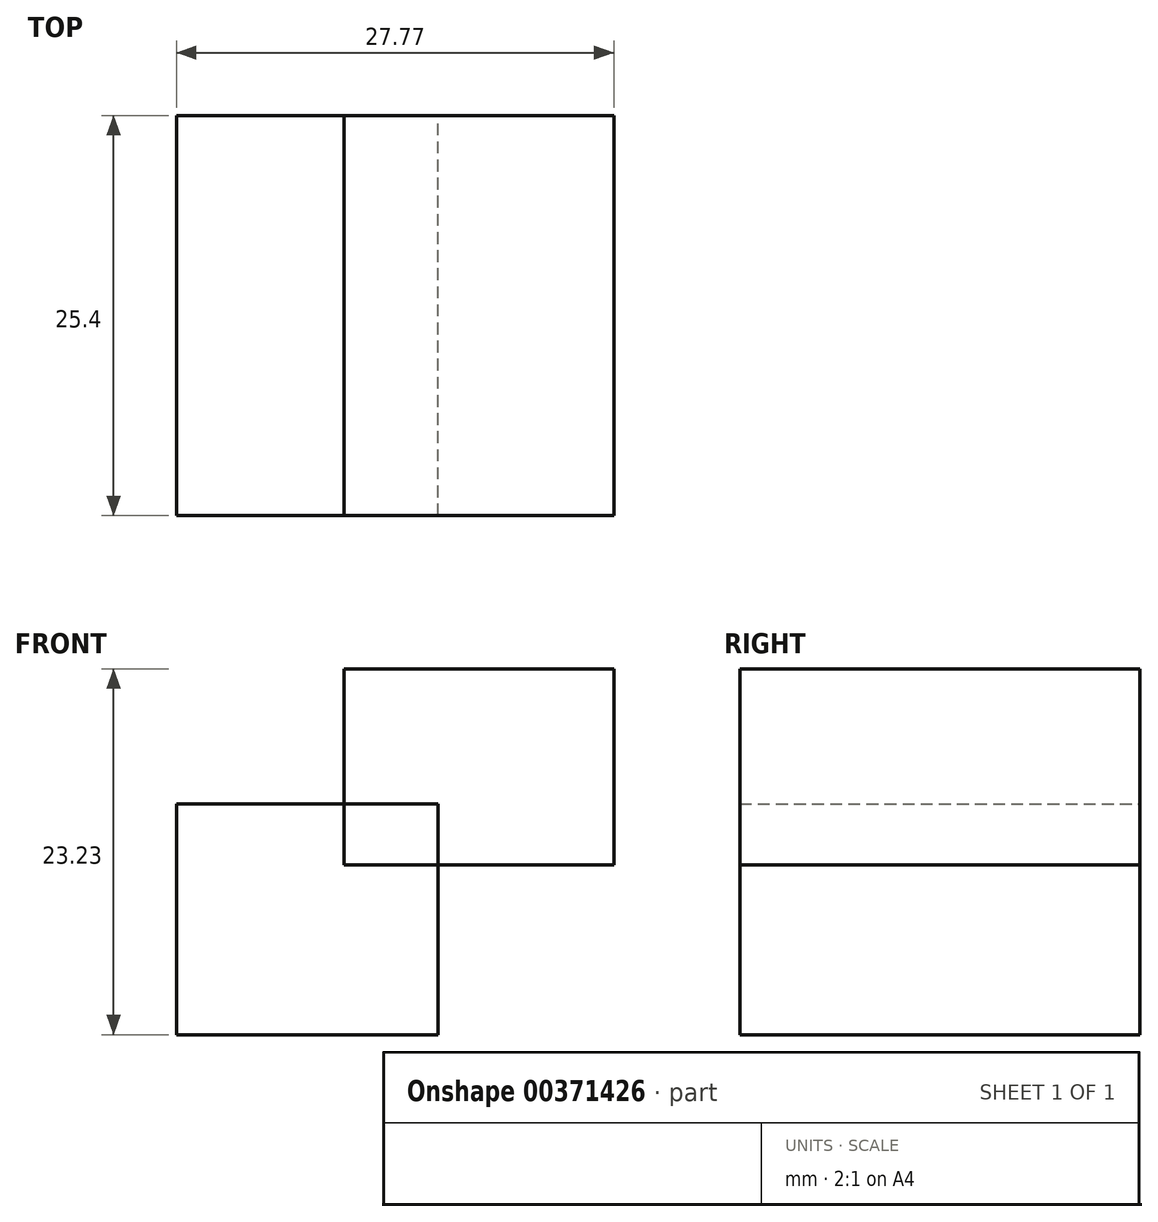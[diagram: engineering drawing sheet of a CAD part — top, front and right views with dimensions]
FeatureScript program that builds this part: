
annotation { "Feature Type Name" : "Feature", "Feature Type Description" : "" }
export const myFeature = defineFeature(function(context is Context, id is Id, definition is map)
    precondition{}
    {
        {
            var Q0;
            Q0=qCreatedBy(makeId("Front.planeOp"),FACE);
            var sketch = newSketch(context, id + "F0", { "sketchPlane" : qUnion([Q0])});
            skLineSegment(sketch, "E0.bottom", {"start": v(0, 0) * mm, "end": v(16.61, 0) * mm});
            skLineSegment(sketch, "E0.top", {"start": v(0, 14.66) * mm, "end": v(16.61, 14.66) * mm});
            skLineSegment(sketch, "E0.left", {"start": v(0, 0) * mm, "end": v(0, 14.66) * mm});
            skLineSegment(sketch, "E0.right", {"start": v(16.61, 0) * mm, "end": v(16.61, 14.66) * mm});
            skLineSegment(sketch, "E1.bottom", {"start": v(10.64, 10.77) * mm, "end": v(27.77, 10.77) * mm});
            skLineSegment(sketch, "E1.top", {"start": v(10.64, 23.23) * mm, "end": v(27.77, 23.23) * mm});
            skLineSegment(sketch, "E1.left", {"start": v(10.64, 10.77) * mm, "end": v(10.64, 23.23) * mm});
            skLineSegment(sketch, "E1.right", {"start": v(27.77, 10.77) * mm, "end": v(27.77, 23.23) * mm});
            skSolve(sketch);
        }
        {
            var Q0;
            {var subQ1=sQuery(id+"F0.wireOp",EDGE,"E0.bottom");Q0=makeQuery(id+"F0.imprint","IMPRINT",FACE,{"disambiguationData":[TD([[makeQuery(id+"F0.imprint","IMPRINT",EDGE,{"derivedFrom":subQ1}),1.0]])]});}
            var Q1;
            {var subQ0=sQuery(id+"F0.wireOp",EDGE,"E0.right");var subQ1=sQuery(id+"F0.wireOp",EDGE,"E0.top");var subQ2=makeQuery(id+"F0.imprint","INTERSECT",VERTEX,{"derivedFrom":[subQ1,subQ0]});Q1=makeQuery(id+"F0.imprint","IMPRINT",FACE,{"disambiguationData":[TD([[makeQuery(id+"F0.imprint","IMPRINT",EDGE,{"disambiguationData":[TD([[subQ2,1.0]])],"derivedFrom":subQ1}),-1.0]])]});}
            extrude(context, id + "F1", {"entities" : qUnion([Q0, Q1]), "depth" : 25.4 * mm});
        }
        {
            var Q0;
            {var subQ0=sQuery(id+"F0.wireOp",EDGE,"E0.right");var subQ1=sQuery(id+"F0.wireOp",EDGE,"E0.top");var subQ2=makeQuery(id+"F0.imprint","INTERSECT",VERTEX,{"derivedFrom":[subQ1,subQ0]});Q0=makeQuery(id+"F0.imprint","IMPRINT",FACE,{"disambiguationData":[TD([[makeQuery(id+"F0.imprint","IMPRINT",EDGE,{"disambiguationData":[TD([[subQ2,1.0]])],"derivedFrom":subQ1}),-1.0]])]});}
            var Q1;
            {var subQ0=sQuery(id+"F0.wireOp",EDGE,"E1.top");Q1=makeQuery(id+"F0.imprint","IMPRINT",FACE,{"disambiguationData":[TD([[makeQuery(id+"F0.imprint","IMPRINT",EDGE,{"derivedFrom":subQ0}),-1.0]])]});}
            extrude(context, id + "F2", {"entities" : qUnion([Q0, Q1]), "depth" : 25.4 * mm});
        }
    });
